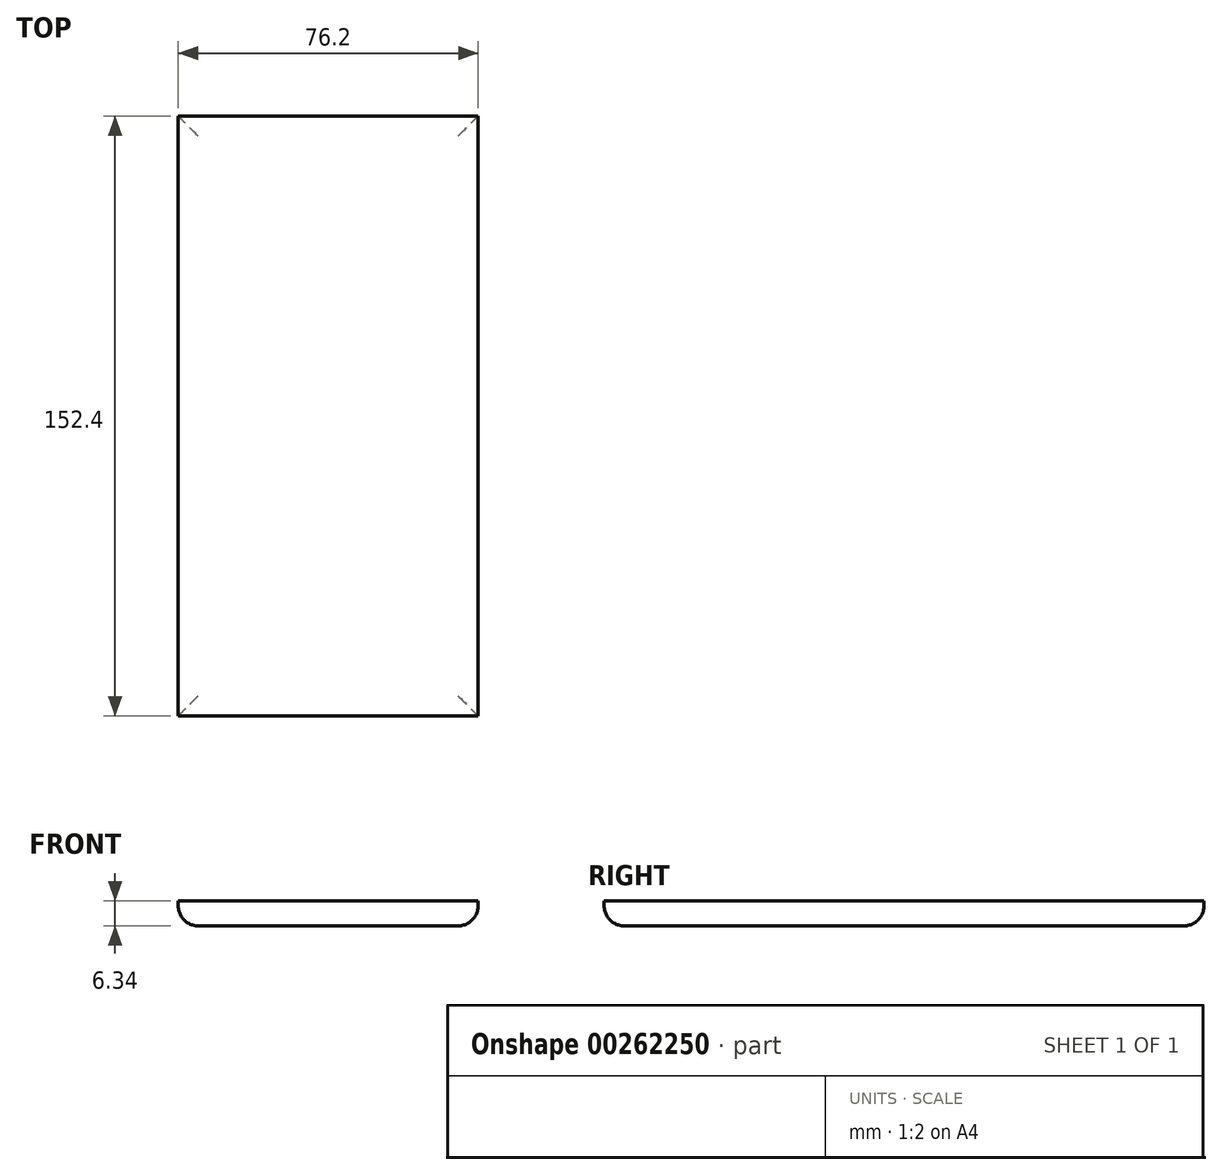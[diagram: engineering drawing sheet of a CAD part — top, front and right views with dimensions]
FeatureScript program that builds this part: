
annotation { "Feature Type Name" : "Feature", "Feature Type Description" : "" }
export const myFeature = defineFeature(function(context is Context, id is Id, definition is map)
    precondition{}
    {
        {
            var Q0;
            Q0=qCreatedBy(makeId("Front.planeOp"),FACE);
            var sketch = newSketch(context, id + "F0", { "sketchPlane" : qUnion([Q0])});
            skLineSegment(sketch, "E0.bottom", {"start": v(38.1, -3.17) * mm, "end": v(-38.1, -3.18) * mm});
            skLineSegment(sketch, "E0.top", {"start": v(38.1, 3.18) * mm, "end": v(-38.1, 3.17) * mm});
            skLineSegment(sketch, "E0.left", {"start": v(38.1, -3.17) * mm, "end": v(38.1, 3.18) * mm});
            skLineSegment(sketch, "E0.right", {"start": v(-38.1, -3.18) * mm, "end": v(-38.1, 3.17) * mm});
            skPoint(sketch, "E0.middle", {"position": v(0, 0) * mm});
            skLineSegment(sketch, "E1.bottom", {"start": v(-38.1, -3.18) * mm, "end": v(-34.3, -3.18) * mm});
            skLineSegment(sketch, "E1.top", {"start": v(-38.1, -53.98) * mm, "end": v(-34.3, -53.98) * mm});
            skLineSegment(sketch, "E1.left", {"start": v(-38.1, -3.18) * mm, "end": v(-38.1, -53.98) * mm});
            skLineSegment(sketch, "E1.right", {"start": v(-34.3, -3.18) * mm, "end": v(-34.3, -53.98) * mm});
            skLineSegment(sketch, "E2.bottom", {"start": v(38.1, -3.17) * mm, "end": v(34.29, -3.17) * mm});
            skLineSegment(sketch, "E2.top", {"start": v(38.1, -53.97) * mm, "end": v(34.29, -53.97) * mm});
            skLineSegment(sketch, "E2.left", {"start": v(38.1, -3.17) * mm, "end": v(38.1, -53.97) * mm});
            skLineSegment(sketch, "E2.right", {"start": v(34.29, -3.17) * mm, "end": v(34.29, -53.97) * mm});
            skSolve(sketch);
        }
        {
            var Q0;
            Q0=makeQuery(id+"F0.imprint","IMPRINT",FACE,{"disambiguationData":[TD([[makeQuery(id+"F0.imprint","IMPRINT",EDGE,{"derivedFrom":sQuery(id+"F0.wireOp",EDGE,"E0.bottom")}),-1.0]])]});
            extrude(context, id + "F1", {"entities" : qUnion([Q0]), "endBound" : BoundingType.SYMMETRIC, "depth" : 152.4 * mm});
        }
        {
            var Q0;
            Q0 = qSketchRegion(id + "F0", true);
            extrude(context, id + "F2", {"entities" : qUnion([Q0]), "operationType" : NewBodyOperationType.ADD, "depth" : 6.35 * mm});
        }
        {
            var Q0;
            {var subQ0=sQuery(id+"F0.wireOp",EDGE,"E2.left");var subQ1=sQuery(id+"F0.wireOp",EDGE,"E0.right");var subQ2=sQuery(id+"F0.wireOp",EDGE,"E0.left");var subQ3=sQuery(id+"F0.wireOp",EDGE,"E0.top");var subQ4=sQuery(id+"F0.wireOp",EDGE,"E0.bottom");var subQ5=sQuery(id+"F0.wireOp",EDGE,"E2.bottom");var subQ6=sQuery(id+"F0.wireOp",EDGE,"E1.bottom");Q0=makeQuery(id+"F2.boolean.opBoolean","SPLIT",EDGE,{"disambiguationData":[TD([makeQuery(id+"F1.opExtrude","CAP_FACE",FACE,{"disambiguationData":[OSD([subQ4,subQ3,subQ2,subQ1,subQ6,subQ5])],"isStart":false})])],"derivedFrom":makeQuery(id+"F1.opExtrude","SWEPT_EDGE",EDGE,{"disambiguationData":[OSD([subQ2,subQ5,subQ0])]})});}
            var Q1;
            Q1=makeQuery(id+"F1.opExtrude","CAP_EDGE",EDGE,{"disambiguationData":[OSD([sQuery(id+"F0.wireOp",EDGE,"E0.bottom"),sQuery(id+"F0.wireOp",EDGE,"E1.bottom"),sQuery(id+"F0.wireOp",EDGE,"E2.bottom")])],"isStart":false});
            var Q2;
            {var subQ0=sQuery(id+"F0.wireOp",EDGE,"E2.left");var subQ1=sQuery(id+"F0.wireOp",EDGE,"E0.right");var subQ2=sQuery(id+"F0.wireOp",EDGE,"E0.left");var subQ3=sQuery(id+"F0.wireOp",EDGE,"E0.top");var subQ4=sQuery(id+"F0.wireOp",EDGE,"E0.bottom");var subQ5=sQuery(id+"F0.wireOp",EDGE,"E2.bottom");var subQ6=sQuery(id+"F0.wireOp",EDGE,"E1.bottom");Q2=makeQuery(id+"F2.boolean.opBoolean","SPLIT",EDGE,{"disambiguationData":[TD([makeQuery(id+"F1.opExtrude","CAP_FACE",FACE,{"disambiguationData":[OSD([subQ4,subQ3,subQ2,subQ1,subQ6,subQ5])],"isStart":true})])],"derivedFrom":makeQuery(id+"F1.opExtrude","SWEPT_EDGE",EDGE,{"disambiguationData":[OSD([subQ2,subQ5,subQ0])]})});}
            var Q3;
            {var subQ0=sQuery(id+"F0.wireOp",EDGE,"E1.left");var subQ1=sQuery(id+"F0.wireOp",EDGE,"E0.right");var subQ2=sQuery(id+"F0.wireOp",EDGE,"E0.left");var subQ3=sQuery(id+"F0.wireOp",EDGE,"E0.top");var subQ4=sQuery(id+"F0.wireOp",EDGE,"E0.bottom");var subQ5=sQuery(id+"F0.wireOp",EDGE,"E2.bottom");var subQ6=sQuery(id+"F0.wireOp",EDGE,"E1.bottom");Q3=makeQuery(id+"F2.boolean.opBoolean","SPLIT",EDGE,{"disambiguationData":[TD([makeQuery(id+"F1.opExtrude","CAP_FACE",FACE,{"disambiguationData":[OSD([subQ4,subQ3,subQ2,subQ1,subQ6,subQ5])],"isStart":false})])],"derivedFrom":makeQuery(id+"F1.opExtrude","SWEPT_EDGE",EDGE,{"disambiguationData":[OSD([subQ1,subQ6,subQ0])]})});}
            var Q4;
            Q4=makeQuery(id+"F1.opExtrude","CAP_EDGE",EDGE,{"disambiguationData":[OSD([sQuery(id+"F0.wireOp",EDGE,"E0.bottom"),sQuery(id+"F0.wireOp",EDGE,"E1.bottom"),sQuery(id+"F0.wireOp",EDGE,"E2.bottom")])],"isStart":true});
            fillet(context, id + "F3", {"entities" : qUnion([Q0, Q1, Q2, Q3, Q4]), "radius" : 5.08 * mm, "tangentPropagation" : true, "allowEdgeOverflow" : false});
        }
        {
            var Q0;
            Q0=qCreatedBy(makeId("Front.planeOp"),FACE);
            var sketch = newSketch(context, id + "F4", { "sketchPlane" : qUnion([Q0])});
            skLineSegment(sketch, "E3.bottom", {"start": v(50.8, -97.8) * mm, "end": v(-50.8, -97.8) * mm});
            skPoint(sketch, "E3.middle", {"position": v(0, 0) * mm});
            skSolve(sketch);
        }
        {
            var Q0;
            Q0=makeQuery(id+"F4.imprint","IMPRINT",FACE,{"disambiguationData":[TD([[makeQuery(id+"F4.imprint","IMPRINT",EDGE,{"derivedFrom":sQuery(id+"F4.wireOp",EDGE,"E3.bottom")}),-1.0]])]});
            var Q1;
            Q1=sQuery(id+"F4.wireOp",EDGE,"E3.right");
            var Q2;
            Q2=sQuery(id+"F4.wireOp",EDGE,"E3.top");
            var Q3;
            Q3=sQuery(id+"F4.wireOp",EDGE,"E3.left");
            var Q4;
            Q4=sQuery(id+"F4.wireOp",EDGE,"E3.bottom");
            extrude(context, id + "F5", {"entities" : qUnion([Q0]), "bodyType" : ToolBodyType.SURFACE, "surfaceEntities" : qUnion([Q1, Q2, Q3, Q4]), "depth" : 6.35 * mm});
        }
    });
